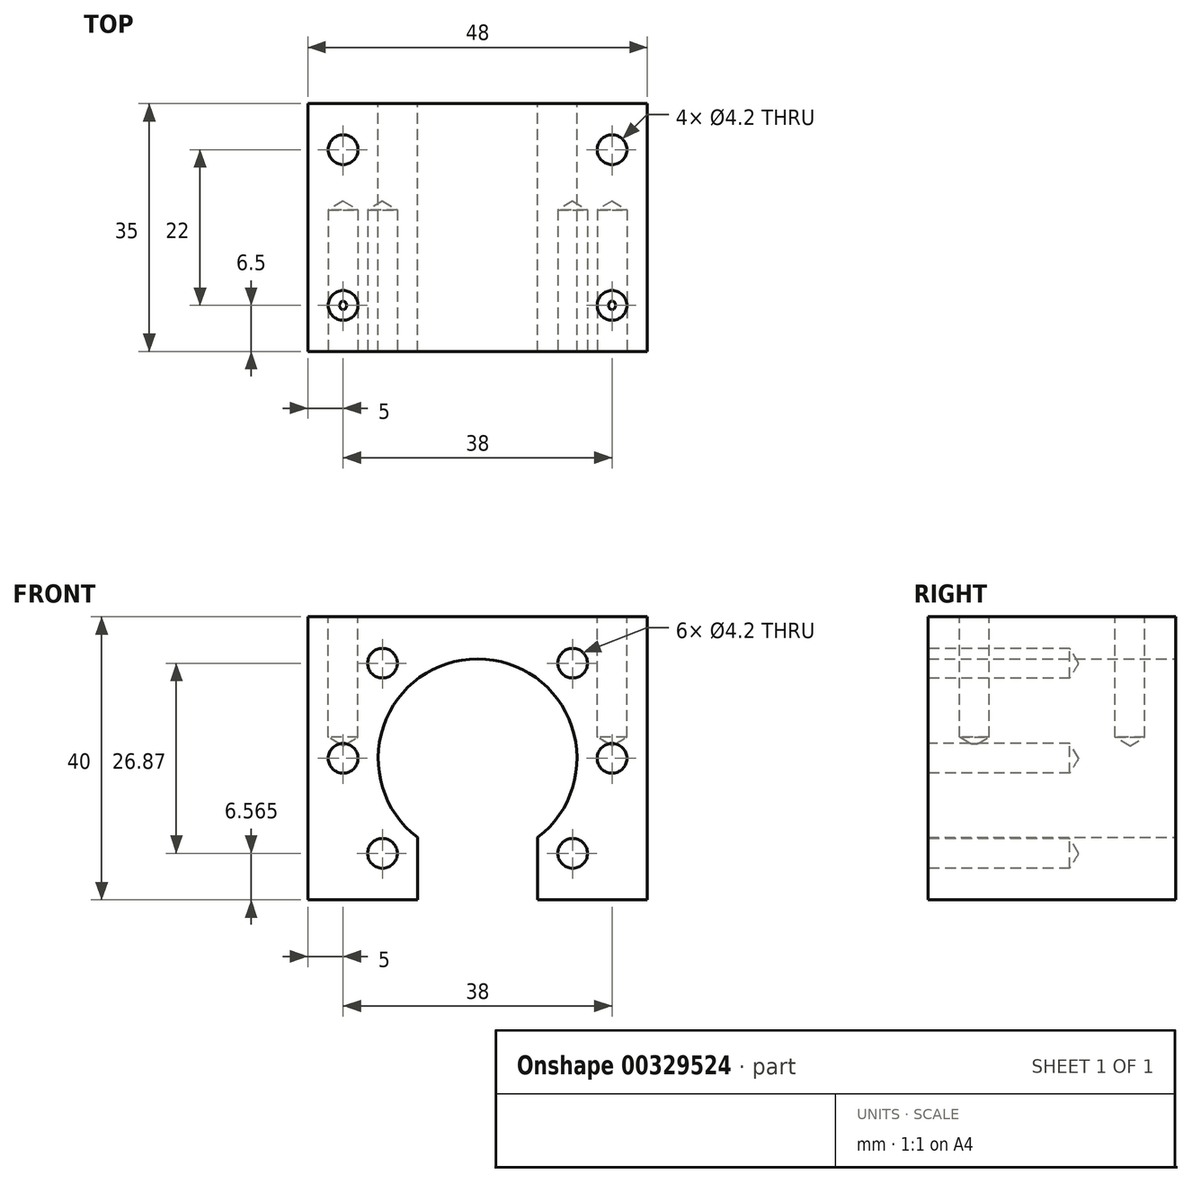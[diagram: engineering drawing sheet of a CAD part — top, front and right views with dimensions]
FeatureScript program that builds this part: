
annotation { "Feature Type Name" : "Feature", "Feature Type Description" : "" }
export const myFeature = defineFeature(function(context is Context, id is Id, definition is map)
    precondition{}
    {
        {
            var Q0;
            Q0=qCreatedBy(makeId("Front.planeOp"),FACE);
            var sketch = newSketch(context, id + "F0", { "sketchPlane" : qUnion([Q0])});
            skLineSegment(sketch, "E0.bottom", {"start": v(24, 20) * mm, "end": v(-24, 20) * mm});
            skLineSegment(sketch, "E0.top", {"start": v(24, -20) * mm, "end": v(8.5, -20) * mm});
            skLineSegment(sketch, "E0.left", {"start": v(24, 20) * mm, "end": v(24, -20) * mm});
            skLineSegment(sketch, "E0.right", {"start": v(-24, 20) * mm, "end": v(-24, -20) * mm});
            skPoint(sketch, "E0.middle", {"position": v(0, 0) * mm});
            skArc(sketch, "E1", {"start": v(8.5, -11.19) * mm, "mid": v(0, 14.05) * mm, "end": v(-8.5, -11.19) * mm});
            skLineSegment(sketch, "E2", {"start": v(-8.5, -11.19) * mm, "end": v(-8.5, -20) * mm});
            skLineSegment(sketch, "E3", {"start": v(8.5, -11.19) * mm, "end": v(8.5, -20) * mm});
            skLineSegment(sketch, "E4.trimOffspring", {"start": v(-8.5, -20) * mm, "end": v(-24, -20) * mm});
            skSolve(sketch);
        }
        {
            var Q0;
            Q0 = qSketchRegion(id + "F0", true);
            extrude(context, id + "F1", {"entities" : qUnion([Q0]), "endBound" : BoundingType.SYMMETRIC, "depth" : 35 * mm});
        }
        {
            var Q0;
            Q0=makeQuery(id+"F1.opExtrude","CAP_FACE",FACE,{"disambiguationData":[OSD([sQuery(id+"F0.wireOp",EDGE,"E0.bottom"),sQuery(id+"F0.wireOp",EDGE,"E0.top"),sQuery(id+"F0.wireOp",EDGE,"E0.left"),sQuery(id+"F0.wireOp",EDGE,"E0.right"),sQuery(id+"F0.wireOp",EDGE,"E1"),sQuery(id+"F0.wireOp",EDGE,"E2"),sQuery(id+"F0.wireOp",EDGE,"E3"),sQuery(id+"F0.wireOp",EDGE,"E4.trimOffspring")])],"isStart":false});
            var sketch = newSketch(context, id + "F2", { "sketchPlane" : qUnion([Q0])});
            skCircle(sketch, "E5", {"center": v(0, 0) * mm, "radius": 19 * mm, "construction": true});
            skPoint(sketch, "E6", {"position": v(-19, 0) * mm});
            skPoint(sketch, "E7", {"position": v(19, 0) * mm});
            skPoint(sketch, "E8", {"position": v(13.44, -13.44) * mm});
            skPoint(sketch, "E9", {"position": v(13.44, 13.44) * mm});
            skPoint(sketch, "E10", {"position": v(-13.44, 13.44) * mm});
            skPoint(sketch, "E11", {"position": v(-13.44, -13.44) * mm});
            skLineSegment(sketch, "E12", {"start": v(13.44, 13.44) * mm, "end": v(0, 0) * mm, "construction": true});
            skLineSegment(sketch, "E13", {"start": v(19, 0) * mm, "end": v(0, 0) * mm, "construction": true});
            skSolve(sketch);
        }
        {
            var Q0;
            Q0=sQuery(id+"F2.wireOp",VERTEX,"E10");
            var Q1;
            Q1=sQuery(id+"F2.wireOp",VERTEX,"E6");
            var Q2;
            Q2=sQuery(id+"F2.wireOp",VERTEX,"E11");
            var Q3;
            Q3=sQuery(id+"F2.wireOp",VERTEX,"E8");
            var Q4;
            Q4=sQuery(id+"F2.wireOp",VERTEX,"E7");
            var Q5;
            Q5=sQuery(id+"F2.wireOp",VERTEX,"E9");
            var Q6;
            Q6=makeQuery(id+"F1.opExtrude","SWEPT_BODY",BODY,{"disambiguationData":[OSD([sQuery(id+"F0.wireOp",EDGE,"E0.bottom"),sQuery(id+"F0.wireOp",EDGE,"E0.top"),sQuery(id+"F0.wireOp",EDGE,"E0.left"),sQuery(id+"F0.wireOp",EDGE,"E0.right"),sQuery(id+"F0.wireOp",EDGE,"E1"),sQuery(id+"F0.wireOp",EDGE,"E2"),sQuery(id+"F0.wireOp",EDGE,"E3"),sQuery(id+"F0.wireOp",EDGE,"E4.trimOffspring")])]});
            hole(context, id + "F3", {"style" : HoleStyle.SIMPLE, "endStyle" : HoleEndStyle.BLIND, "standardTappedOrClearance" : lookupTablePath({ "standard" : "ISO", "engagement" : "75%", "pitch" : "0.8 mm", "size" : "M5", "type" : "Tapped" }), "standardBlindInLast" : lookupTablePath({ "standard" : "ISO", "engagement" : "75%", "pitch" : "0.8 mm", "size" : "M5", "type" : "Tapped" }), "holeDiameter" : 4.2 * mm, "showTappedDepth" : true, "holeDepth" : 20 * mm, "tappedDepth" : 17.6 * mm, "tapClearance" : 3, "locations" : qUnion([Q0, Q1, Q2, Q3, Q4, Q5]), "scope" : qUnion([Q6]), "majorDiameter" : 5 * mm});
        }
        {
            var Q0;
            Q0=makeQuery(id+"F1.opExtrude","SWEPT_FACE",FACE,{"disambiguationData":[OSD([sQuery(id+"F0.wireOp",EDGE,"E0.bottom")])]});
            var sketch = newSketch(context, id + "F4", { "sketchPlane" : qUnion([Q0])});
            skPoint(sketch, "E14", {"position": v(-19, 11) * mm});
            skPoint(sketch, "E15", {"position": v(-19, -11) * mm});
            skPoint(sketch, "E16", {"position": v(19, -11) * mm});
            skPoint(sketch, "E17", {"position": v(19, 11) * mm});
            skSolve(sketch);
        }
        {
            var Q0;
            Q0=sQuery(id+"F4.wireOp",VERTEX,"E14");
            var Q1;
            Q1=sQuery(id+"F4.wireOp",VERTEX,"E15");
            var Q2;
            Q2=sQuery(id+"F4.wireOp",VERTEX,"E16");
            var Q3;
            Q3=sQuery(id+"F4.wireOp",VERTEX,"E17");
            var Q4;
            Q4=makeQuery(id+"F1.opExtrude","SWEPT_BODY",BODY,{"disambiguationData":[OSD([sQuery(id+"F0.wireOp",EDGE,"E0.bottom"),sQuery(id+"F0.wireOp",EDGE,"E0.top"),sQuery(id+"F0.wireOp",EDGE,"E0.left"),sQuery(id+"F0.wireOp",EDGE,"E0.right"),sQuery(id+"F0.wireOp",EDGE,"E1"),sQuery(id+"F0.wireOp",EDGE,"E2"),sQuery(id+"F0.wireOp",EDGE,"E3"),sQuery(id+"F0.wireOp",EDGE,"E4.trimOffspring")])]});
            hole(context, id + "F5", {"style" : HoleStyle.SIMPLE, "endStyle" : HoleEndStyle.BLIND, "standardTappedOrClearance" : lookupTablePath({ "standard" : "ISO", "engagement" : "75%", "pitch" : "0.8 mm", "size" : "M5", "type" : "Tapped" }), "standardBlindInLast" : lookupTablePath({ "standard" : "ISO", "engagement" : "75%", "pitch" : "0.8 mm", "size" : "M5", "type" : "Tapped" }), "holeDiameter" : 4.2 * mm, "showTappedDepth" : true, "holeDepth" : 17 * mm, "tappedDepth" : 14.6 * mm, "tapClearance" : 3, "locations" : qUnion([Q0, Q1, Q2, Q3]), "scope" : qUnion([Q4]), "majorDiameter" : 5 * mm});
        }
    });
